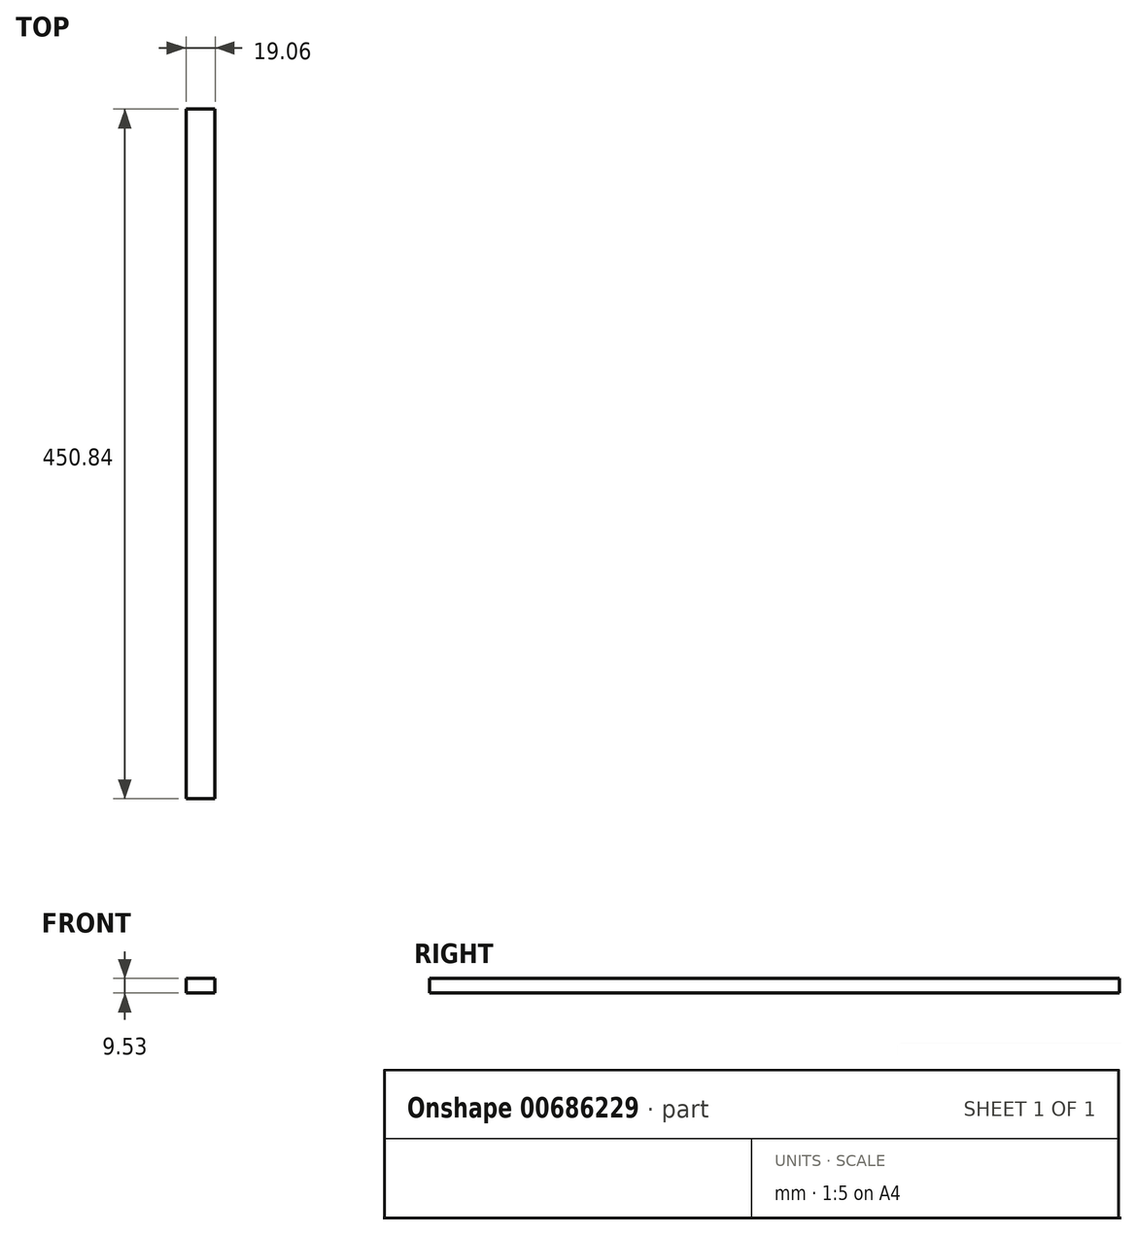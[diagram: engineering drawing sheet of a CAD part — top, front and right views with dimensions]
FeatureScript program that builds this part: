
annotation { "Feature Type Name" : "Feature", "Feature Type Description" : "" }
export const myFeature = defineFeature(function(context is Context, id is Id, definition is map)
    precondition{}
    {
        {
            var Q0;
            Q0=qCreatedBy(makeId("Front.planeOp"),FACE);
            var sketch = newSketch(context, id + "F0", { "sketchPlane" : qUnion([Q0])});
            skLineSegment(sketch, "E0.top", {"start": v(9.52, 9.53) * mm, "end": v(-9.53, 9.53) * mm});
            skLineSegment(sketch, "E0.left", {"start": v(9.52, 0) * mm, "end": v(9.52, 9.53) * mm});
            skLineSegment(sketch, "E0.right", {"start": v(-9.53, 0) * mm, "end": v(-9.53, 9.53) * mm});
            skLineSegment(sketch, "E1", {"start": v(-9.53, 0) * mm, "end": v(9.53, 0) * mm});
            skSolve(sketch);
        }
        {
            var Q0;
            Q0 = qSketchRegion(id + "F0", true);
            extrude(context, id + "F1", {"entities" : qUnion([Q0]), "endBound" : BoundingType.SYMMETRIC, "depth" : 450.85 * mm, "offsetDistance" : 25.4 * mm});
        }
    });
